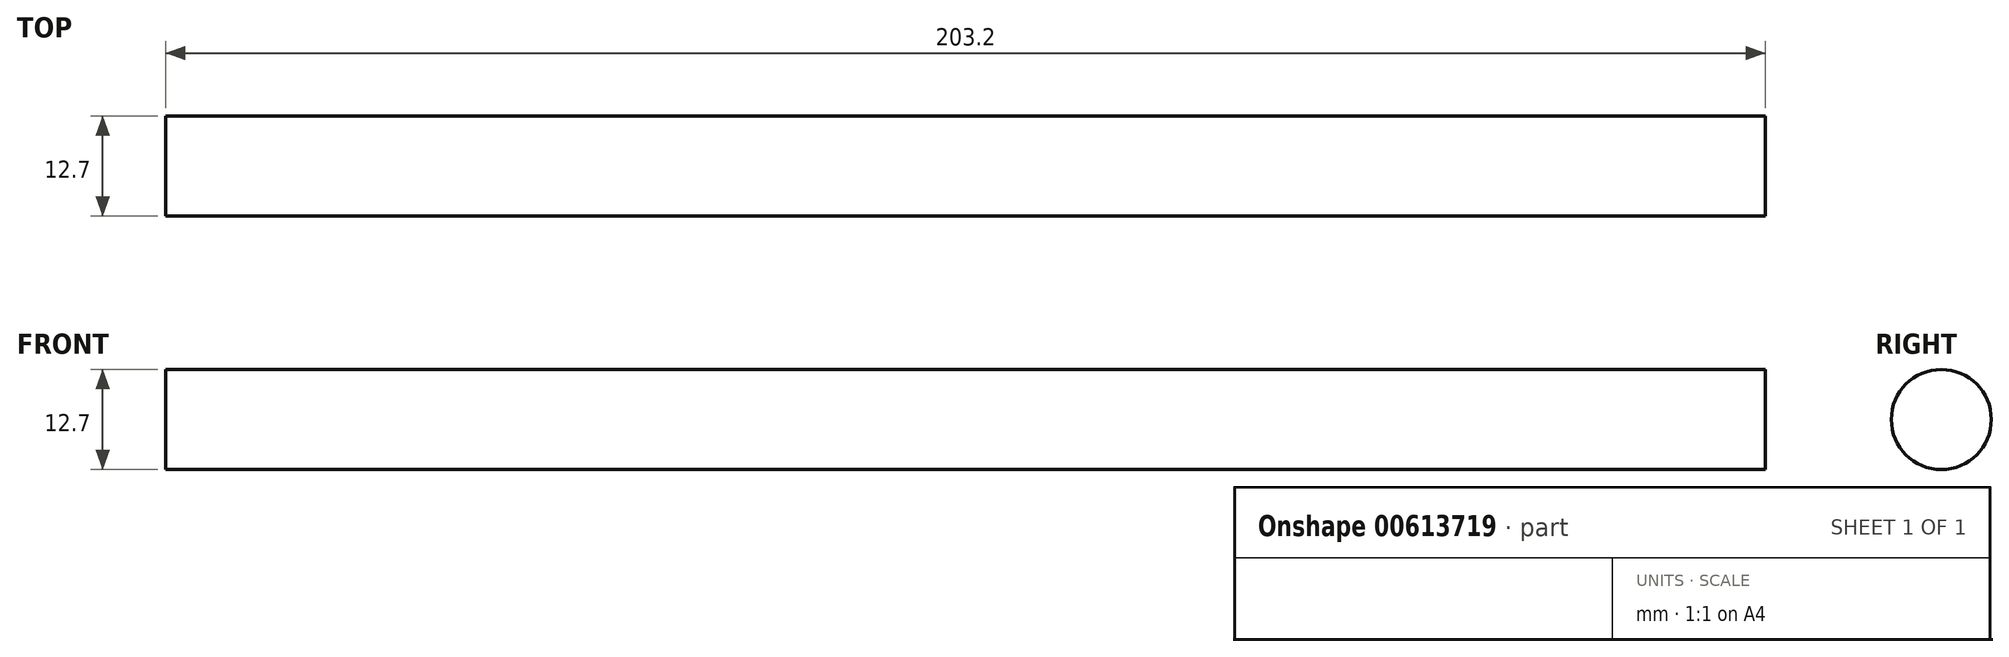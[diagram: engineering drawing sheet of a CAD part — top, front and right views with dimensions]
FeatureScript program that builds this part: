
annotation { "Feature Type Name" : "Feature", "Feature Type Description" : "" }
export const myFeature = defineFeature(function(context is Context, id is Id, definition is map)
    precondition{}
    {
        {
            var Q0;
            Q0=qCreatedBy(makeId("Right.planeOp"),FACE);
            var sketch = newSketch(context, id + "F0", { "sketchPlane" : qUnion([Q0])});
            skCircle(sketch, "E0", {"center": v(0, 0) * mm, "radius": 6.35 * mm});
            skSolve(sketch);
        }
        {
            var Q0;
            Q0 = qSketchRegion(id + "F0", true);
            extrude(context, id + "F1", {"entities" : qUnion([Q0]), "endBound" : BoundingType.SYMMETRIC, "depth" : 203.2 * mm, "offsetDistance" : 25.4 * mm});
        }
    });
